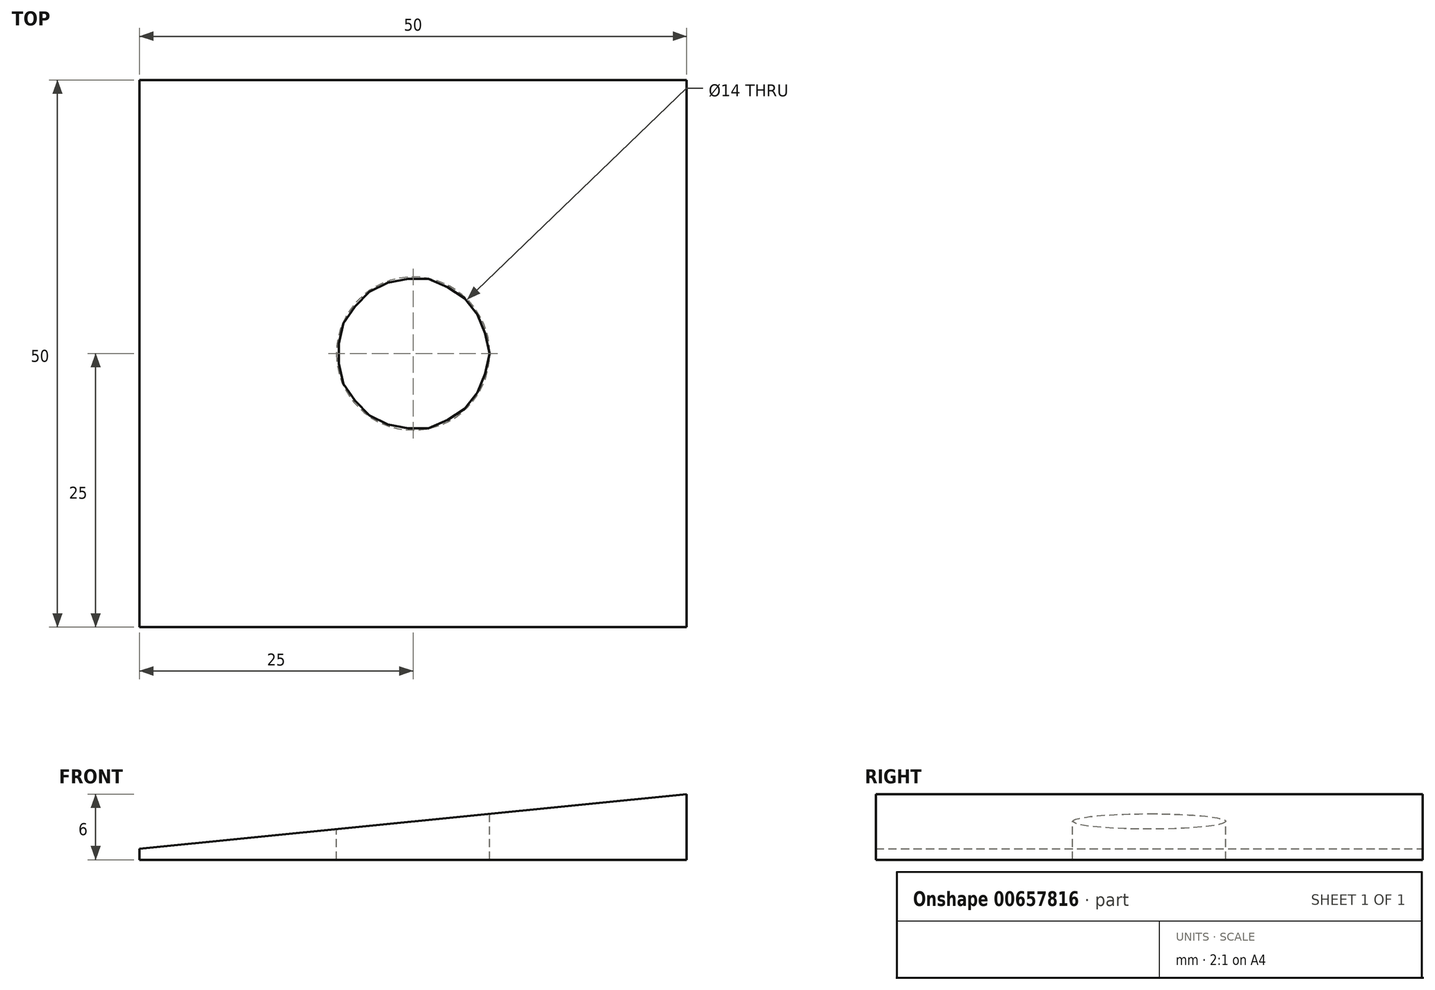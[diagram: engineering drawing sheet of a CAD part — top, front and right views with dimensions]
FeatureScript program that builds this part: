
annotation { "Feature Type Name" : "Feature", "Feature Type Description" : "" }
export const myFeature = defineFeature(function(context is Context, id is Id, definition is map)
    precondition{}
    {
        {
            var Q0;
            Q0=qCreatedBy(makeId("Front.planeOp"),FACE);
            var sketch = newSketch(context, id + "F0", { "sketchPlane" : qUnion([Q0])});
            skLineSegment(sketch, "E0", {"start": v(25, 0) * mm, "end": v(-25, 0) * mm});
            skLineSegment(sketch, "E1", {"start": v(-25, 0) * mm, "end": v(-25, 1) * mm});
            skLineSegment(sketch, "E2", {"start": v(-25, 1) * mm, "end": v(25, 6) * mm});
            skLineSegment(sketch, "E3", {"start": v(25, 6) * mm, "end": v(25, 0) * mm});
            skSolve(sketch);
        }
        {
            var Q0;
            Q0=makeQuery(id+"F0.imprint","IMPRINT",FACE,{"disambiguationData":[TD([[makeQuery(id+"F0.imprint","IMPRINT",EDGE,{"derivedFrom":sQuery(id+"F0.wireOp",EDGE,"E0")}),-1.0]])]});
            extrude(context, id + "F1", {"entities" : qUnion([Q0]), "depth" : 25 * mm, "offsetDistance" : 25 * mm, "hasSecondDirection" : true, "secondDirectionOppositeDirection" : true, "secondDirectionDepth" : 25 * mm});
        }
        {
            var Q0;
            Q0=qCreatedBy(makeId("Top.planeOp"),FACE);
            var sketch = newSketch(context, id + "F2", { "sketchPlane" : qUnion([Q0])});
            skCircle(sketch, "E4", {"center": v(0, 0) * mm, "radius": 7 * mm});
            skSolve(sketch);
        }
        {
            var Q0;
            Q0=makeQuery(id+"F2.imprint","IMPRINT",FACE,{"disambiguationData":[TD([[makeQuery(id+"F2.imprint","IMPRINT",EDGE,{"derivedFrom":sQuery(id+"F2.wireOp",EDGE,"E4")}),1.0]])]});
            extrude(context, id + "F3", {"entities" : qUnion([Q0]), "operationType" : NewBodyOperationType.REMOVE, "oppositeDirection" : true, "depth" : 25 * mm, "offsetDistance" : 25 * mm, "hasSecondDirection" : true, "secondDirectionOppositeDirection" : false, "secondDirectionDepth" : 32.4 * mm});
        }
    });
